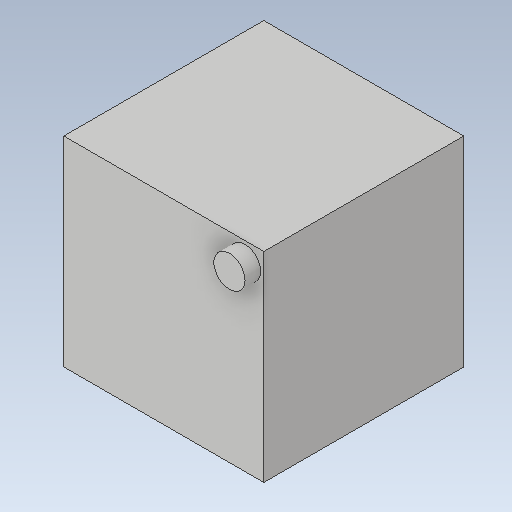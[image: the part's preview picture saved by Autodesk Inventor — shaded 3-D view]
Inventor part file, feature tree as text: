
AUTODESK INVENTOR PART (.ipt)
format: ipt  version: 2020 (Build 240168000, 168)  size: 96,768 bytes
history: native  units: mm
features: extrude x2, sketch x2
ambient origin geometry x8: Origin, YZ Plane, XZ Plane, XY Plane, X Axis, Y Axis, Z Axis, Center Point
bodies: Solid1 (feature_tree)
feature tree (4):
  extrude  "Extrusion1"  Depth=320.0mm
  extrude  "Extrusion3"  Depth=25.0mm
  sketch  "Sketch1"  dims[d0=320.0mm d1=320.0mm]
  sketch  "Sketch3"  dims[d2=320.0mm d3=0.0mm d6=50.0mm d7=30.0mm d8=30.0mm d9=25.0mm d10=0.0mm]
